# Revit family: RN 90019 Optifitt-Serra-Winkel
name_source: partatom
category: Rohrformteile
units: mm (PartAtom-declared; Revit-internal decimal feet)

## family parameters
Arbeitsebenenbasiert = Nein
Beim Laden mit Abzugskörper schneiden = Nein
Bemaßung runder Anschluss = Durchmesser verwenden
Gemeinsam genutzt = Nein
Immer vertikal = Ja
Teiletyp = Bogen

## types (2) — shared parameters
1.010.00.2 Blattnummer der Richtlinie = 29
1.010.00.3 Ausgabedatum (Monat) der Richtlinie = 201308
1.010.00.4 Herstellername = R. Nussbaum AG
1.010.00.5 Revisionsdatum der Datei = 20190521
1.010.00.6 Webadresse des Herstellers = http://www.nussbaum.ch
1.100.00.4 Produktbezeichnung = Versorgung
1.110.00.2 Index = 3
1.110.00.4 Produktbezeichnung = Optifitt-Serra
1.960/3L.00.8 Link (URL) = https://www.nussbaum.ch
29.700.00.4 Produktname = Optifitt-Serra-Winkel, mit Wandflansch
29.700.00.5 Produktkennung = 2
29.700.00.6 Querschnittsform = 1
29.700.00.7 Nennweitensystem = DN
29.700.00.8 Nenndrucksystem = PN
29.710.02.4 Nenndruck = 16
29.710.02.5 max. zul. Überdruck [hPa] = 1600
29.710.02.7 max. zul. Dauer-Betriebsdruck [hPa] = 1600
29.710.02.9 max. zul. Dauer-Betriebstemperatur [°C] = 90
Connector Visibility = Nein
EnclosingSpace Visibility = Nein
Hersteller = R. Nussbaum AG
URL = https://www.nussbaum.ch

## per-type parameters (varying)
| type | 1.800.00.3 TGA-Nummer | 1.800.00.4 Kommentarfeld | 1.810.00.3 Hersteller-Bestellnummer | 1.810.00.4 DATANORM-Nummer | 1.810.00.5 StLB-Nummer | 1.810.00.6 GTIN-Nummer | 29.710.02.10 Formstück-Gewicht [kg] | 29.710.02.3 Benennung | CONNECTOR0_DIAMETER_dY_0r | CONNECTOR0_dY_00 | CONNECTOR0_dY_01 | CONNECTOR0_ref_dY | CONNECTOR1_DIAMETER_dX_0r | CONNECTOR1_dX_00 | CONNECTOR1_dX_01 | CONNECTOR1_ref_dX | Modell | R. Nussbaum AG 90019.04 de Visibility | R. Nussbaum AG 90019.05 de Visibility | Typenkommentare |
| DN=20 | 01900300000000000000000000000000000000000000000010000000000000000002 | 90019.05, Optifitt-Serra-Winkel, mit Wandflansch, DN=20, L=35, Rp=¾ | 90019.05 | 90019.05 |  | 7612945705297 | 0.208 | Optifitt-Serra-Winkel, mit Wandflansch, DN=20, L=35, Rp=¾ | 20 mm  [stored 0.0656168 ft] | 20 mm  [stored 0.0656168 ft] | 35 mm | 20 mm  [stored 0.0656168 ft] | 20 mm  [stored 0.0656168 ft] | 35 mm | 20 mm  [stored 0.0656168 ft] | 20 mm  [stored 0.0656168 ft] | 90019.05 | Nein | Ja | Optifitt-Serra-Winkel DN=20 |
| DN=15 | 01900300000000000000000000000000000000000000000010000000000000000001 | 90019.04, Optifitt-Serra-Winkel, mit Wandflansch, DN=15, L=36, Rp=½ | 90019.04 | 90019.04 | 212.572 | 7612945033093 | 0.148 | Optifitt-Serra-Winkel, mit Wandflansch, DN=15, L=36, Rp=½ | 15 mm | 23 mm  [stored 0.0754593 ft] | 36 mm | 23 mm  [stored 0.0754593 ft] | 15 mm | 31 mm | 18 mm  [stored 0.0590551 ft] | 18 mm  [stored 0.0590551 ft] | 90019.04 | Ja | Nein | Optifitt-Serra-Winkel DN=15 |

note: [stored X ft] marks values corroborated as IEEE doubles in the binary element streams (Revit-internal decimal feet)

## geometry (parser evidence)
native form markers: Sweep x2
no freeform markers — native parametric forms only
